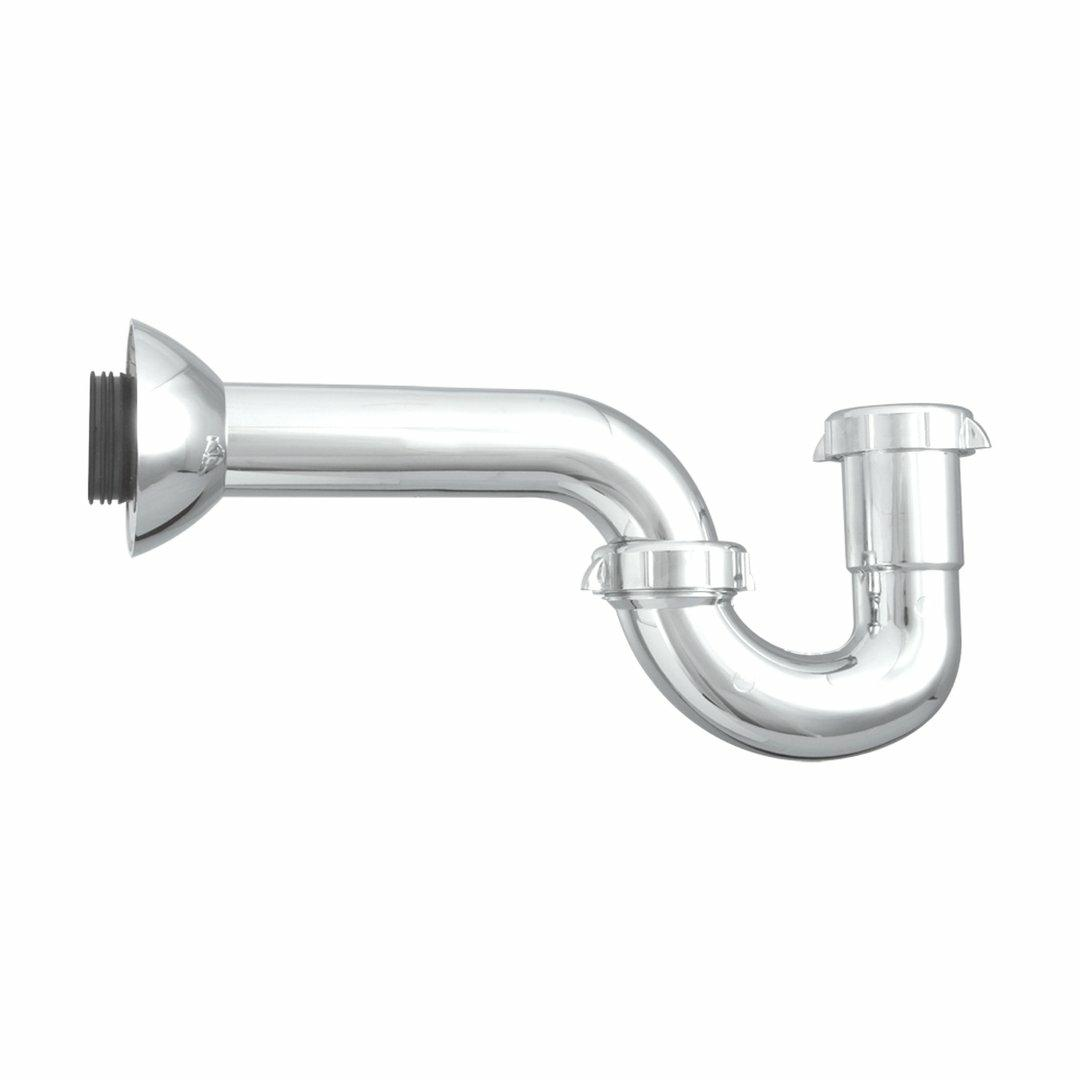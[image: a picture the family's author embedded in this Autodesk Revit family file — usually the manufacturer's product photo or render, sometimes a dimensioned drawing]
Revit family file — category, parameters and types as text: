
# Revit family: 01-4018-15 LAVAMANOS VESSEL GEB
name_source: partatom
category: Plumbing Fixtures
revit_build: Autodesk Revit 2018 (Build: 20170223_1515(x64)
units: mm (PartAtom-declared; Revit-internal decimal feet)

## family parameters
Cut with Voids When Loaded = No
Host = Face
OmniClass Number = 23.31.11.00
Part Type = Normal
Room Calculation Point = No
Round Connector Dimension = Use Diameter
Shared = No

## types (1)
- 01-4018-15
    Alto = 150 mm  [stored 0.492126 ft]
    Ancho = 550 mm
    CW Connection = Yes
    Ceramica = Porcelana
    Default Elevation = 0 mm  [stored 0 ft]
    Description = Lavamanos tipo vessel
    HW Connection = Yes
    Largo = 420 mm
    Link Ficha Tecnica = http://infotecnica.gricol.com
    Manufacturer = Gricol
    Model = 01-4018-15
    Product Name = LAVAMANOS VESSEL GEB
    Push = push cromado
    Type Image = LAVAMANOS VESSEL GEB FOTO.JPG
    URL = https://www.gricol.com
    Vent Connection = No
    Waste Connection = No

note: [stored X ft] marks values corroborated as IEEE doubles in the binary element streams (Revit-internal decimal feet)

## geometry (parser evidence)
native form markers: Blend x8, Sweep x12
no freeform markers — native parametric forms only
